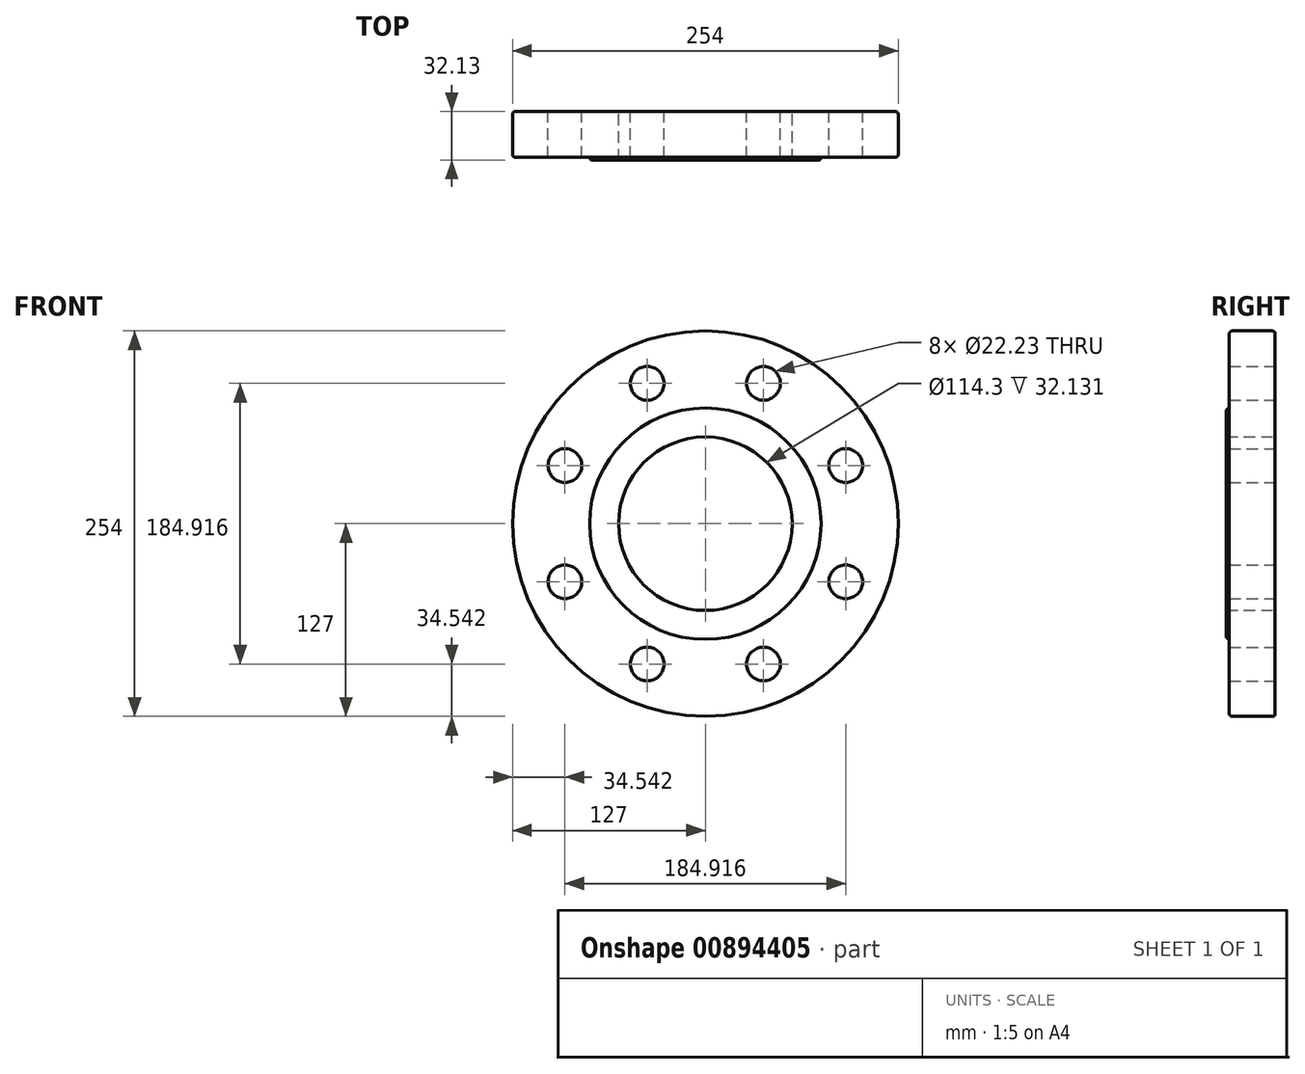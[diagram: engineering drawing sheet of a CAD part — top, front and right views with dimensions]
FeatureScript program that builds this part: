
annotation { "Feature Type Name" : "Feature", "Feature Type Description" : "" }
export const myFeature = defineFeature(function(context is Context, id is Id, definition is map)
    precondition{}
    {
        {
            var Q0;
            Q0=qCreatedBy(makeId("Front.planeOp"),FACE);
            var sketch = newSketch(context, id + "F0", { "sketchPlane" : qUnion([Q0])});
            skCircle(sketch, "E0", {"center": v(0, 0) * mm, "radius": 127 * mm});
            skCircle(sketch, "E1", {"center": v(0, 0) * mm, "radius": 57.15 * mm});
            skCircle(sketch, "E2", {"center": v(0, 0) * mm, "radius": 100.08 * mm, "construction": true});
            skLineSegment(sketch, "E3", {"start": v(0, 0) * mm, "end": v(0, 176.37) * mm, "construction": true});
            skLineSegment(sketch, "E4", {"start": v(0, 0) * mm, "end": v(67.82, 163.74) * mm, "construction": true});
            skCircle(sketch, "E5", {"center": v(38.3, 92.46) * mm, "radius": 11.11 * mm});
            skCircle(sketch, "E6.1.0", {"center": v(-38.3, 92.46) * mm, "radius": 11.11 * mm});
            skCircle(sketch, "E6.2.0", {"center": v(-92.46, 38.3) * mm, "radius": 11.11 * mm});
            skCircle(sketch, "E6.3.0", {"center": v(-92.46, -38.3) * mm, "radius": 11.11 * mm});
            skCircle(sketch, "E6.4.0", {"center": v(-38.3, -92.46) * mm, "radius": 11.11 * mm});
            skCircle(sketch, "E6.5.0", {"center": v(38.3, -92.46) * mm, "radius": 11.11 * mm});
            skCircle(sketch, "E6.6.0", {"center": v(92.46, -38.3) * mm, "radius": 11.11 * mm});
            skCircle(sketch, "E6.7.0", {"center": v(92.46, 38.3) * mm, "radius": 11.11 * mm});
            skSolve(sketch);
        }
        {
            var Q0;
            Q0 = qSketchRegion(id + "F0", true);
            extrude(context, id + "F1", {"entities" : qUnion([Q0]), "depth" : 30.23 * mm, "offsetDistance" : 25.4 * mm});
        }
        {
            var Q0;
            Q0=makeQuery(id+"F1.opExtrude","CAP_FACE",FACE,{"disambiguationData":[OSD([sQuery(id+"F0.wireOp",EDGE,"E0"),sQuery(id+"F0.wireOp",EDGE,"E1"),sQuery(id+"F0.wireOp",EDGE,"E5"),sQuery(id+"F0.wireOp",EDGE,"E6.1.0"),sQuery(id+"F0.wireOp",EDGE,"E6.2.0"),sQuery(id+"F0.wireOp",EDGE,"E6.3.0"),sQuery(id+"F0.wireOp",EDGE,"E6.4.0"),sQuery(id+"F0.wireOp",EDGE,"E6.5.0"),sQuery(id+"F0.wireOp",EDGE,"E6.6.0"),sQuery(id+"F0.wireOp",EDGE,"E6.7.0")])],"isStart":false});
            var sketch = newSketch(context, id + "F2", { "sketchPlane" : qUnion([Q0])});
            skCircle(sketch, "E7", {"center": v(0, 0) * mm, "radius": 57.15 * mm});
            skCircle(sketch, "E8", {"center": v(0, 0) * mm, "radius": 76.2 * mm});
            skSolve(sketch);
        }
        {
            var Q0;
            Q0 = qSketchRegion(id + "F2", true);
            extrude(context, id + "F3", {"entities" : qUnion([Q0]), "operationType" : NewBodyOperationType.ADD, "depth" : 1.9 * mm, "offsetDistance" : 25.4 * mm});
        }
        {
            var Q0;
            Q0=makeQuery(id+"F1.opExtrude","CAP_EDGE",EDGE,{"disambiguationData":[OSD([sQuery(id+"F0.wireOp",EDGE,"E0")])],"isStart":true});
            var Q1;
            Q1=makeQuery(id+"F1.opExtrude","CAP_EDGE",EDGE,{"disambiguationData":[OSD([sQuery(id+"F0.wireOp",EDGE,"E0")])],"isStart":false});
            var Q2;
            Q2=makeQuery(id+"F3.opExtrude","CAP_EDGE",EDGE,{"disambiguationData":[OSD([sQuery(id+"F2.wireOp",EDGE,"E8")])],"isStart":false});
            fillet(context, id + "F4", {"entities" : qUnion([Q0, Q1, Q2]), "radius" : 1.9 * mm, "tangentPropagation" : true, "allowEdgeOverflow" : false});
        }
    });
